# Revit family: 11.2(14,16)kW
name_source: partatom
category: Mechanical Equipment
revit_build: Autodesk Revit 2013 (Build: 20120221_2030(x64)
units: mm (PartAtom-declared; Revit-internal decimal feet)

## types (4) — shared parameters
Condensation = air
Depth = 770 mm
Description = High efficiency air cooled
Gas = R32/R410A
Gas pipe = 15.9 mm
Gas pipe Radius = 7.95 mm  [stored 0.0260827 ft]
Height = 245 mm  [stored 0.803806 ft]
Installation = Indoor installation
Liquid pipe = 9.52 mm
Liquid pipe Radius = 4.76 mm
Machine material = grilles：ABS/HIPS
Maximum Fuse Amps = 15 A
Power supply = 220-240V, 50/60Hz
Series = VRF IDU
Width = 1510 mm
clearance access behind = 200 mm  [stored 0.656168 ft]
clearance access left = 200 mm  [stored 0.656168 ft]
clearance access right = 300 mm
zero-valued in all types: clearance access front

## per-type parameters (varying)
| type | Air  Flow | Cooling Capacity | Cooling Power Input | Heating Capacity | Heating Power Input | Minimum Circuit Amps | Net Weight |
| 11.2kW | 1950/1817 /1683/1550/1417/1283/1150 m3/h | 11.20 kW | 138 W | 12.50 kW | 138 W | 2 A | 37.00 kg |
| 14kW | 2105/1971 /1837/1703/1568/1434/1300 m3/h | 14.00 kW | 172 W | 16.00 kW | 172 W | 2 A | 39.00 kg |
| 16kW | 2350/2160/2015/1871/1776/1533/1400 m3/h | 16.00 kW | 210 W | 18.00 kW | 210 W | 3 A | 39.00 kg |
| 12.5kW | 2105/1971/1837/1703/1568/1434/1300 m3/h | 12.50 kW | 172 W | 14.00 kW | 172 W | 2 A | 39.00 kg |

note: column(s) folded — value = type name in every type: Model

note: [stored X ft] marks values corroborated as IEEE doubles in the binary element streams (Revit-internal decimal feet)

## geometry (parser evidence)
native form markers: Sweep x8
no freeform markers — native parametric forms only
